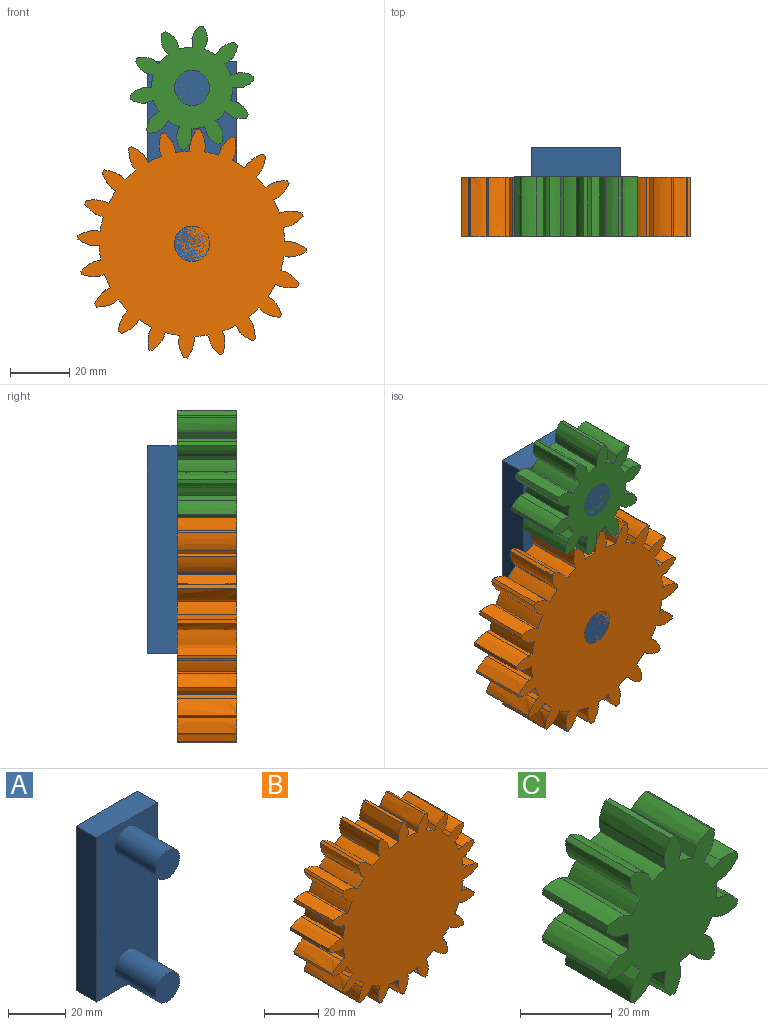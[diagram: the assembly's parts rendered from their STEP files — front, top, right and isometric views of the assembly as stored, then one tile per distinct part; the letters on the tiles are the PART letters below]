
ASSEMBLY  parts=3 mates=2
PART A: 10 faces, bbox 30x30x70 mm
  f0: plane 30x10mm, normal (0,0,1), area 300mm2, adj f1,f3,f4,f5
  f1: plane 70x10mm, normal (-1,0,0), area 700mm2, adj f0,f2,f4,f5
  f2: plane 30x10mm, normal (0,0,-1), area 300mm2, adj f1,f3,f4,f5
  f3: plane 70x10mm, normal (1,0,0), area 700mm2, adj f0,f2,f4,f5
  f4: plane 70x30mm, normal (0,-1,0), area 1879.8mm2, adj f0,f1,f2,f3,f6,f8
  f5: plane 70x30mm, normal (0,1,0), area 2100mm2, adj f0,f1,f2,f3
  f6: cylinder r=5.89mm len=20mm, axis (0,1,0), area 740.4mm2, adj f4,f7
  f7: plane 11.78x11.78mm, normal (0,-1,0), area 109.1mm2, adj f6
  f8: cylinder r=5.95mm len=20mm, axis (0,1,0), area 747.4mm2, adj f4,f9
  f9: plane 11.9x11.9mm, normal (0,-1,0), area 111.1mm2, adj f8
PART B: 122 faces, bbox 77x20x77 mm
  f0: extruded ~20x5.71mm, area 121.9mm2, adj f1,f4,f5,f6
  f1: plane 20x1.68mm, normal (-1,0,-0.08), area 33.8mm2, adj f0,f5,f6,f7
  f2: plane 20x1.68mm, normal (1,0,-0.08), area 33.8mm2, adj f3,f5,f6,f121
  f3: extruded ~20x5.71mm, area 121.9mm2, adj f2,f4,f5,f6
  f4: cylinder r=38.5mm len=20mm, axis (0,1,0), area 25.2mm2, adj f0,f3,f5,f6
  f5: plane 77x77mm, normal (0,-1,0), area 3646.6mm2, adj f0,f1,f2,f3,f4,f7,f8,f9
  f6: plane 77x77mm, normal (0,1,0), area 3646.6mm2, adj f0,f1,f2,f3,f4,f7,f8,f9
  f7: cylinder r=31.2mm len=20mm, axis (0,1,0), area 98mm2, adj f1,f5,f6,f10
  f8: extruded ~20x6.03mm, area 121.9mm2, adj f5,f6,f9,f12
  f9: plane 20x1.56mm, normal (-0.92,0,-0.38), area 33.8mm2, adj f5,f6,f8,f13
  f10: plane 20x1.64mm, normal (0.97,0,0.23), area 33.8mm2, adj f5,f6,f7,f11
  f11: extruded ~20x4.83mm, area 121.9mm2, adj f5,f6,f10,f12
  f12: cylinder r=38.5mm len=20mm, axis (0,1,0), area 25.2mm2, adj f5,f6,f8,f11
  f13: cylinder r=31.2mm len=20mm, axis (0,1,0), area 98mm2, adj f5,f6,f9,f16
  f14: extruded ~20x5.76mm, area 121.9mm2, adj f5,f6,f15,f18
  f15: plane 20x1.28mm, normal (-0.76,0,-0.65), area 33.8mm2, adj f5,f6,f14,f19
  f16: plane 20x1.44mm, normal (0.85,0,0.52), area 33.8mm2, adj f5,f6,f13,f17
  f17: extruded ~20x4.93mm, area 121.9mm2, adj f5,f6,f16,f18
  f18: cylinder r=38.5mm len=20mm, axis (0,1,0), area 25.2mm2, adj f5,f6,f14,f17
  f19: cylinder r=31.2mm len=20mm, axis (0,1,0), area 98mm2, adj f5,f6,f15,f22
  f20: extruded ~20x4.93mm, area 121.9mm2, adj f5,f6,f21,f24
  f21: plane 20x1.44mm, normal (-0.52,0,-0.85), area 33.8mm2, adj f5,f6,f20,f25
  f22: plane 20x1.28mm, normal (0.65,0,0.76), area 33.8mm2, adj f5,f6,f19,f23
  f23: extruded ~20x5.76mm, area 121.9mm2, adj f5,f6,f22,f24
  f24: cylinder r=38.5mm len=20mm, axis (0,1,0), area 25.2mm2, adj f5,f6,f20,f23
  f25: cylinder r=31.2mm len=20mm, axis (0,1,0), area 98mm2, adj f5,f6,f21,f28
  f26: extruded ~20x4.83mm, area 121.9mm2, adj f5,f6,f27,f30
  f27: plane 20x1.64mm, normal (-0.23,0,-0.97), area 33.8mm2, adj f5,f6,f26,f31
  f28: plane 20x1.56mm, normal (0.38,0,0.92), area 33.8mm2, adj f5,f6,f25,f29
  f29: extruded ~20x6.03mm, area 121.9mm2, adj f5,f6,f28,f30
  f30: cylinder r=38.5mm len=20mm, axis (0,1,0), area 25.2mm2, adj f5,f6,f26,f29
  f31: cylinder r=31.2mm len=20mm, axis (0,1,0), area 98mm2, adj f5,f6,f27,f34
  f32: extruded ~20x5.71mm, area 121.9mm2, adj f5,f6,f33,f36
  f33: plane 20x1.68mm, normal (0.08,0,-1), area 33.8mm2, adj f5,f6,f32,f37
  f34: plane 20x1.68mm, normal (0.08,0,1), area 33.8mm2, adj f5,f6,f31,f35
  f35: extruded ~20x5.71mm, area 121.9mm2, adj f5,f6,f34,f36
  f36: cylinder r=38.5mm len=20mm, axis (0,1,0), area 25.2mm2, adj f5,f6,f32,f35
  f37: cylinder r=31.2mm len=20mm, axis (0,1,0), area 98mm2, adj f5,f6,f33,f40
  f38: extruded ~20x6.03mm, area 121.9mm2, adj f5,f6,f39,f42
  f39: plane 20x1.56mm, normal (0.38,0,-0.92), area 33.8mm2, adj f5,f6,f38,f43
  f40: plane 20x1.64mm, normal (-0.23,0,0.97), area 33.8mm2, adj f5,f6,f37,f41
  f41: extruded ~20x4.83mm, area 121.9mm2, adj f5,f6,f40,f42
  f42: cylinder r=38.5mm len=20mm, axis (0,1,0), area 25.2mm2, adj f5,f6,f38,f41
  f43: cylinder r=31.2mm len=20mm, axis (0,1,0), area 98mm2, adj f5,f6,f39,f46
  f44: extruded ~20x5.76mm, area 121.9mm2, adj f5,f6,f45,f48
  f45: plane 20x1.28mm, normal (0.65,0,-0.76), area 33.8mm2, adj f5,f6,f44,f49
  f46: plane 20x1.44mm, normal (-0.52,0,0.85), area 33.8mm2, adj f5,f6,f43,f47
  f47: extruded ~20x4.93mm, area 121.9mm2, adj f5,f6,f46,f48
  f48: cylinder r=38.5mm len=20mm, axis (0,1,0), area 25.2mm2, adj f5,f6,f44,f47
  f49: cylinder r=31.2mm len=20mm, axis (0,1,0), area 98mm2, adj f5,f6,f45,f52
  f50: extruded ~20x4.93mm, area 121.9mm2, adj f5,f6,f51,f54
  f51: plane 20x1.44mm, normal (0.85,0,-0.52), area 33.8mm2, adj f5,f6,f50,f55
  f52: plane 20x1.28mm, normal (-0.76,0,0.65), area 33.8mm2, adj f5,f6,f49,f53
  f53: extruded ~20x5.76mm, area 121.9mm2, adj f5,f6,f52,f54
  f54: cylinder r=38.5mm len=20mm, axis (0,1,0), area 25.2mm2, adj f5,f6,f50,f53
  f55: cylinder r=31.2mm len=20mm, axis (0,1,0), area 98mm2, adj f5,f6,f51,f58
  f56: extruded ~20x4.83mm, area 121.9mm2, adj f5,f6,f57,f60
  f57: plane 20x1.64mm, normal (0.97,0,-0.23), area 33.8mm2, adj f5,f6,f56,f61
  f58: plane 20x1.56mm, normal (-0.92,0,0.38), area 33.8mm2, adj f5,f6,f55,f59
  f59: extruded ~20x6.03mm, area 121.9mm2, adj f5,f6,f58,f60
  f60: cylinder r=38.5mm len=20mm, axis (0,1,0), area 25.2mm2, adj f5,f6,f56,f59
  f61: cylinder r=31.2mm len=20mm, axis (0,1,0), area 98mm2, adj f5,f6,f57,f64
  f62: extruded ~20x5.71mm, area 121.9mm2, adj f5,f6,f63,f66
  f63: plane 20x1.68mm, normal (1,0,0.08), area 33.8mm2, adj f5,f6,f62,f67
  f64: plane 20x1.68mm, normal (-1,0,0.08), area 33.8mm2, adj f5,f6,f61,f65
  f65: extruded ~20x5.71mm, area 121.9mm2, adj f5,f6,f64,f66
  f66: cylinder r=38.5mm len=20mm, axis (0,1,0), area 25.2mm2, adj f5,f6,f62,f65
  f67: cylinder r=31.2mm len=20mm, axis (0,1,0), area 98mm2, adj f5,f6,f63,f70
  f68: extruded ~20x6.03mm, area 121.9mm2, adj f5,f6,f69,f72
  f69: plane 20x1.56mm, normal (0.92,0,0.38), area 33.8mm2, adj f5,f6,f68,f73
  f70: plane 20x1.64mm, normal (-0.97,0,-0.23), area 33.8mm2, adj f5,f6,f67,f71
  f71: extruded ~20x4.83mm, area 121.9mm2, adj f5,f6,f70,f72
  f72: cylinder r=38.5mm len=20mm, axis (0,1,0), area 25.2mm2, adj f5,f6,f68,f71
  f73: cylinder r=31.2mm len=20mm, axis (0,1,0), area 98mm2, adj f5,f6,f69,f76
  f74: extruded ~20x5.76mm, area 121.9mm2, adj f5,f6,f75,f78
  f75: plane 20x1.28mm, normal (0.76,0,0.65), area 33.8mm2, adj f5,f6,f74,f79
  f76: plane 20x1.44mm, normal (-0.85,0,-0.52), area 33.8mm2, adj f5,f6,f73,f77
  f77: extruded ~20x4.93mm, area 121.9mm2, adj f5,f6,f76,f78
  f78: cylinder r=38.5mm len=20mm, axis (0,1,0), area 25.2mm2, adj f5,f6,f74,f77
  f79: cylinder r=31.2mm len=20mm, axis (0,1,0), area 98mm2, adj f5,f6,f75,f82
  f80: extruded ~20x4.93mm, area 121.9mm2, adj f5,f6,f81,f84
  f81: plane 20x1.44mm, normal (0.52,0,0.85), area 33.8mm2, adj f5,f6,f80,f85
  f82: plane 20x1.28mm, normal (-0.65,0,-0.76), area 33.8mm2, adj f5,f6,f79,f83
  f83: extruded ~20x5.76mm, area 121.9mm2, adj f5,f6,f82,f84
  f84: cylinder r=38.5mm len=20mm, axis (0,1,0), area 25.2mm2, adj f5,f6,f80,f83
  f85: cylinder r=31.2mm len=20mm, axis (0,1,0), area 98mm2, adj f5,f6,f81,f88
  f86: extruded ~20x4.83mm, area 121.9mm2, adj f5,f6,f87,f90
  f87: plane 20x1.64mm, normal (0.23,0,0.97), area 33.8mm2, adj f5,f6,f86,f91
  f88: plane 20x1.56mm, normal (-0.38,0,-0.92), area 33.8mm2, adj f5,f6,f85,f89
  f89: extruded ~20x6.03mm, area 121.9mm2, adj f5,f6,f88,f90
  f90: cylinder r=38.5mm len=20mm, axis (0,1,0), area 25.2mm2, adj f5,f6,f86,f89
  f91: cylinder r=31.2mm len=20mm, axis (0,1,0), area 98mm2, adj f5,f6,f87,f94
  f92: extruded ~20x5.71mm, area 121.9mm2, adj f5,f6,f93,f96
  f93: plane 20x1.68mm, normal (-0.08,0,1), area 33.8mm2, adj f5,f6,f92,f97
  f94: plane 20x1.68mm, normal (-0.08,0,-1), area 33.8mm2, adj f5,f6,f91,f95
  f95: extruded ~20x5.71mm, area 121.9mm2, adj f5,f6,f94,f96
  f96: cylinder r=38.5mm len=20mm, axis (0,1,0), area 25.2mm2, adj f5,f6,f92,f95
  f97: cylinder r=31.2mm len=20mm, axis (0,1,0), area 98mm2, adj f5,f6,f93,f100
  f98: extruded ~20x6.03mm, area 121.9mm2, adj f5,f6,f99,f102
  f99: plane 20x1.56mm, normal (-0.38,0,0.92), area 33.8mm2, adj f5,f6,f98,f103
  f100: plane 20x1.64mm, normal (0.23,0,-0.97), area 33.8mm2, adj f5,f6,f97,f101
  f101: extruded ~20x4.83mm, area 121.9mm2, adj f5,f6,f100,f102
  f102: cylinder r=38.5mm len=20mm, axis (0,1,0), area 25.2mm2, adj f5,f6,f98,f101
  f103: cylinder r=31.2mm len=20mm, axis (0,1,0), area 98mm2, adj f5,f6,f99,f106
  f104: extruded ~20x5.76mm, area 121.9mm2, adj f5,f6,f105,f108
  f105: plane 20x1.28mm, normal (-0.65,0,0.76), area 33.8mm2, adj f5,f6,f104,f109
  f106: plane 20x1.44mm, normal (0.52,0,-0.85), area 33.8mm2, adj f5,f6,f103,f107
  f107: extruded ~20x4.93mm, area 121.9mm2, adj f5,f6,f106,f108
  f108: cylinder r=38.5mm len=20mm, axis (0,1,0), area 25.2mm2, adj f5,f6,f104,f107
  f109: cylinder r=31.2mm len=20mm, axis (0,1,0), area 98mm2, adj f5,f6,f105,f112
  f110: extruded ~20x4.93mm, area 121.9mm2, adj f5,f6,f111,f114
  f111: plane 20x1.44mm, normal (-0.85,0,0.52), area 33.8mm2, adj f5,f6,f110,f115
  f112: plane 20x1.28mm, normal (0.76,0,-0.65), area 33.8mm2, adj f5,f6,f109,f113
  f113: extruded ~20x5.76mm, area 121.9mm2, adj f5,f6,f112,f114
  f114: cylinder r=38.5mm len=20mm, axis (0,1,0), area 25.2mm2, adj f5,f6,f110,f113
  f115: cylinder r=31.2mm len=20mm, axis (0,1,0), area 98mm2, adj f5,f6,f111,f118
  f116: extruded ~20x4.83mm, area 121.9mm2, adj f5,f6,f117,f120
  f117: plane 20x1.64mm, normal (-0.97,0,0.23), area 33.8mm2, adj f5,f6,f116,f121
  f118: plane 20x1.56mm, normal (0.92,0,-0.38), area 33.8mm2, adj f5,f6,f115,f119
  f119: extruded ~20x6.03mm, area 121.9mm2, adj f5,f6,f118,f120
  f120: cylinder r=38.5mm len=20mm, axis (0,1,0), area 25.2mm2, adj f5,f6,f116,f119
  f121: cylinder r=31.2mm len=20mm, axis (0,1,0), area 98mm2, adj f2,f5,f6,f117
PART C: 62 faces, bbox 40.4x20x42 mm
  f0: plane 20x2.71mm, normal (-0.99,0,-0.16), area 54.9mm2, adj f4,f5,f6,f7
  f1: plane 20x2.71mm, normal (0.99,0,-0.16), area 54.9mm2, adj f2,f5,f6,f61
  f2: extruded ~20x4.75mm, area 103.8mm2, adj f1,f3,f5,f6
  f3: cylinder r=21mm len=20mm, axis (0,1,0), area 28.3mm2, adj f2,f4,f5,f6
  f4: extruded ~20x4.75mm, area 103.8mm2, adj f0,f3,f5,f6
  f5: plane 42x40.36mm, normal (0,-1,0), area 896.4mm2, adj f0,f1,f2,f3,f4,f7,f8,f9
  f6: plane 42x40.36mm, normal (0,1,0), area 896.4mm2, adj f0,f1,f2,f3,f4,f7,f8,f9
  f7: cylinder r=13.7mm len=20mm, axis (0,1,0), area 86.1mm2, adj f0,f5,f6,f9
  f8: plane 20x1.94mm, normal (-0.71,0,-0.71), area 54.9mm2, adj f5,f6,f12,f13
  f9: plane 20x2.45mm, normal (0.89,0,0.45), area 54.9mm2, adj f5,f6,f7,f10
  f10: extruded ~20x4.3mm, area 103.8mm2, adj f5,f6,f9,f11
  f11: cylinder r=21mm len=20mm, axis (0,1,0), area 28.3mm2, adj f5,f6,f10,f12
  f12: extruded ~20x4.94mm, area 103.8mm2, adj f5,f6,f8,f11
  f13: cylinder r=13.7mm len=20mm, axis (0,1,0), area 86.1mm2, adj f5,f6,f8,f15
  f14: plane 20x2.71mm, normal (-0.16,0,-0.99), area 54.9mm2, adj f5,f6,f18,f19
  f15: plane 20x2.45mm, normal (0.45,0,0.89), area 54.9mm2, adj f5,f6,f13,f16
  f16: extruded ~20x5.09mm, area 103.8mm2, adj f5,f6,f15,f17
  f17: cylinder r=21mm len=20mm, axis (0,1,0), area 28.3mm2, adj f5,f6,f16,f18
  f18: extruded ~20x3.94mm, area 103.8mm2, adj f5,f6,f14,f17
  f19: cylinder r=13.7mm len=20mm, axis (0,1,0), area 86.1mm2, adj f5,f6,f14,f21
  f20: plane 20x2.45mm, normal (0.45,0,-0.89), area 54.9mm2, adj f5,f6,f24,f25
  f21: plane 20x2.71mm, normal (-0.16,0,0.99), area 54.9mm2, adj f5,f6,f19,f22
  f22: extruded ~20x3.94mm, area 103.8mm2, adj f5,f6,f21,f23
  f23: cylinder r=21mm len=20mm, axis (0,1,0), area 28.3mm2, adj f5,f6,f22,f24
  f24: extruded ~20x5.09mm, area 103.8mm2, adj f5,f6,f20,f23
  f25: cylinder r=13.7mm len=20mm, axis (0,1,0), area 86.1mm2, adj f5,f6,f20,f27
  f26: plane 20x2.45mm, normal (0.89,0,-0.45), area 54.9mm2, adj f5,f6,f30,f31
  f27: plane 20x1.94mm, normal (-0.71,0,0.71), area 54.9mm2, adj f5,f6,f25,f28
  f28: extruded ~20x4.94mm, area 103.8mm2, adj f5,f6,f27,f29
  f29: cylinder r=21mm len=20mm, axis (0,1,0), area 28.3mm2, adj f5,f6,f28,f30
  f30: extruded ~20x4.3mm, area 103.8mm2, adj f5,f6,f26,f29
  f31: cylinder r=13.7mm len=20mm, axis (0,1,0), area 86.1mm2, adj f5,f6,f26,f33
  f32: plane 20x2.71mm, normal (0.99,0,0.16), area 54.9mm2, adj f5,f6,f36,f37
  f33: plane 20x2.71mm, normal (-0.99,0,0.16), area 54.9mm2, adj f5,f6,f31,f34
  f34: extruded ~20x4.75mm, area 103.8mm2, adj f5,f6,f33,f35
  f35: cylinder r=21mm len=20mm, axis (0,1,0), area 28.3mm2, adj f5,f6,f34,f36
  f36: extruded ~20x4.75mm, area 103.8mm2, adj f5,f6,f32,f35
  f37: cylinder r=13.7mm len=20mm, axis (0,1,0), area 86.1mm2, adj f5,f6,f32,f39
  f38: plane 20x1.94mm, normal (0.71,0,0.71), area 54.9mm2, adj f5,f6,f42,f43
  f39: plane 20x2.45mm, normal (-0.89,0,-0.45), area 54.9mm2, adj f5,f6,f37,f40
  f40: extruded ~20x4.3mm, area 103.8mm2, adj f5,f6,f39,f41
  f41: cylinder r=21mm len=20mm, axis (0,1,0), area 28.3mm2, adj f5,f6,f40,f42
  f42: extruded ~20x4.94mm, area 103.8mm2, adj f5,f6,f38,f41
  f43: cylinder r=13.7mm len=20mm, axis (0,1,0), area 86.1mm2, adj f5,f6,f38,f45
  f44: plane 20x2.71mm, normal (0.16,0,0.99), area 54.9mm2, adj f5,f6,f48,f49
  f45: plane 20x2.45mm, normal (-0.45,0,-0.89), area 54.9mm2, adj f5,f6,f43,f46
  f46: extruded ~20x5.09mm, area 103.8mm2, adj f5,f6,f45,f47
  f47: cylinder r=21mm len=20mm, axis (0,1,0), area 28.3mm2, adj f5,f6,f46,f48
  f48: extruded ~20x3.94mm, area 103.8mm2, adj f5,f6,f44,f47
  f49: cylinder r=13.7mm len=20mm, axis (0,1,0), area 86.1mm2, adj f5,f6,f44,f51
  f50: plane 20x2.45mm, normal (-0.45,0,0.89), area 54.9mm2, adj f5,f6,f54,f55
  f51: plane 20x2.71mm, normal (0.16,0,-0.99), area 54.9mm2, adj f5,f6,f49,f52
  f52: extruded ~20x3.94mm, area 103.8mm2, adj f5,f6,f51,f53
  f53: cylinder r=21mm len=20mm, axis (0,1,0), area 28.3mm2, adj f5,f6,f52,f54
  f54: extruded ~20x5.09mm, area 103.8mm2, adj f5,f6,f50,f53
  f55: cylinder r=13.7mm len=20mm, axis (0,1,0), area 86.1mm2, adj f5,f6,f50,f57
  f56: plane 20x2.45mm, normal (-0.89,0,0.45), area 54.9mm2, adj f5,f6,f60,f61
  f57: plane 20x1.94mm, normal (0.71,0,-0.71), area 54.9mm2, adj f5,f6,f55,f58
  f58: extruded ~20x4.94mm, area 103.8mm2, adj f5,f6,f57,f59
  f59: cylinder r=21mm len=20mm, axis (0,1,0), area 28.3mm2, adj f5,f6,f58,f60
  f60: extruded ~20x4.3mm, area 103.8mm2, adj f5,f6,f56,f59
  f61: cylinder r=13.7mm len=20mm, axis (0,1,0), area 86.1mm2, adj f1,f5,f6,f56
PLACE A t=(48.13,11.68,60.63)mm
PLACE B rot(axis=(0,-1,0),14.7deg) t=(146.17,1.68,141.71)mm
PLACE C rot(axis=(0,-1,0),27deg) t=(146.17,1.68,194.21)mm
MATE revolute B.f4 <-> A.f8  axis (0,-1,0) through (146.17,-18.32,141.71)mm
MATE revolute C.f3 <-> A.f6  axis (0,-1,0) through (146.17,-18.32,194.21)mm
